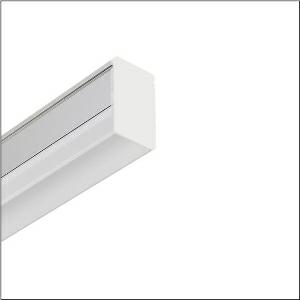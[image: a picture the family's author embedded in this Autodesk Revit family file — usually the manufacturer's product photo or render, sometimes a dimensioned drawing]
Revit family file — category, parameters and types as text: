
# Revit family: siluette_r__41-f_51lp327km20af_698e
name_source: partatom
category: Lighting Fixtures
units: mm (PartAtom-declared; Revit-internal decimal feet)

## family parameters
Cut with Voids When Loaded = No
Host = Face
Light Source = No
Part Type = Normal
Room Calculation Point = No
Round Connector Dimension = Use Diameter
Shared = No

## types (1)
- --- (1 x LED, 2000 lm, 16 W, 5000K)
    Apparent Load = 16 VA
    CIE Flux Codes = 37 66 87 87 100
    Color Rendering = 80
    Color Temperature = 5000K
    Default Elevation = 1800 mm
    Description = Siluette® 41-F, batten luminaire, primary optical cover: cover, of PC, frosted, light emission: direct distribution, primary light characteristic: symmetric, installation type: surface-mounted, LED, rated luminous flux: 2.000lm, luminous efficacy: 125lm/W, light colour: 830/840/850, colour temperature: 3000/4000/5000K, control gear: ON/OFF, with terminal, 2-pole, mains connection: 220..240V, AC, 50/60Hz, rated input power: 16W, housing, of aluminium, silver, length: 1.180mm, width: 25mm, height: 44mm, end cap, of PC, white, protection rating (complete): IP20, insulation class (complete): insulation class II (safety insulation), certification: CE, permissible operating ambient temperature: -20..+40°C, packaging unit: 1 piece
    Height = 44 mm
    Lamp = 1 x LED
    Lamp Light Flux = 2000 lm
    Lamp Power = 16 W
    Lamp count = 1
    Length = 1180 mm
    Luminous efficacy = 125 lm/W
    Manufacturer = Siteco
    ModVariant = No
    Model = 51LP327KM20AF
    Mounting Place = Ceiling
    Mounting Type = Surface mounted
    Number of Poles = 1
    OnlyDefault = Yes
    Power Factor = 1
    Product Name = Siluette® 41-F
    Product group = batten luminaire
    ProductGroupID = 304
    Protection Class = Protection class II
    Protection Degree = IP 20
    RLX_Detail_Level = 1
    RLX_Emergency_Light_Flux = 0 lm
    RLX_Emergency_Type = 0
    RLX_Emergency_Type_DB = No
    RlxData = <blob elided: 28417 chars, md5=4b1508d2>
    Socket = socket
    Standby Power = 0 W
    System Light Flux = 2000 lm
    System Power = 16 W
    Type Comments = individual setting: colour temperature 5000K
    Type Image = l_1007255.jpg
    URL = http://relux.com
    VarID = @adj_042789
    Voltage = 0 V
    Weight = 0.00 kg
    Width = 25 mm  [stored 0.082021 ft]

note: [stored X ft] marks values corroborated as IEEE doubles in the binary element streams (Revit-internal decimal feet)

## geometry (parser evidence)
native form markers: Blend x4, Sweep x13
no freeform markers — native parametric forms only
